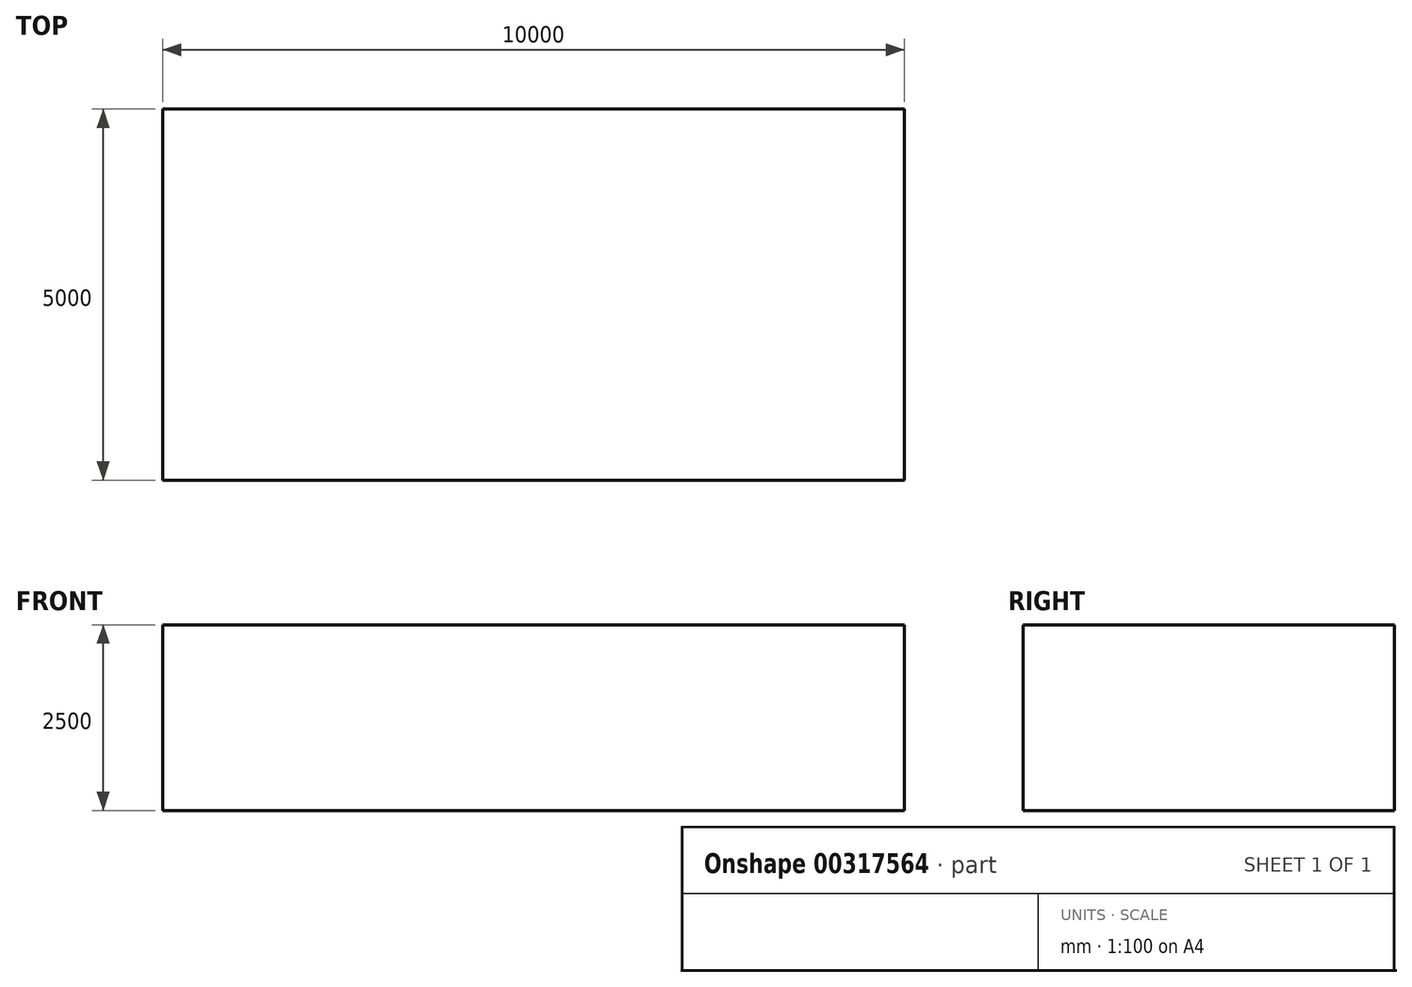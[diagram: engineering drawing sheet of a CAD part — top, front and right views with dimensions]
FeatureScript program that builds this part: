
annotation { "Feature Type Name" : "Feature", "Feature Type Description" : "" }
export const myFeature = defineFeature(function(context is Context, id is Id, definition is map)
    precondition{}
    {
        {
            var Q0;
            Q0=qCreatedBy(makeId("Front.planeOp"),FACE);
            var sketch = newSketch(context, id + "F0", { "sketchPlane" : qUnion([Q0])});
            skLineSegment(sketch, "E0.bottom", {"start": v(-4999.46, -1331.01) * mm, "end": v(5000.54, -1331.01) * mm});
            skLineSegment(sketch, "E0.top", {"start": v(-4999.46, -3831.01) * mm, "end": v(5000.54, -3831.01) * mm});
            skLineSegment(sketch, "E0.left", {"start": v(-4999.46, -1331.01) * mm, "end": v(-4999.46, -3831.01) * mm});
            skLineSegment(sketch, "E0.right", {"start": v(5000.54, -1331.01) * mm, "end": v(5000.54, -3831.01) * mm});
            skSolve(sketch);
        }
        {
            var Q0;
            Q0 = qSketchRegion(id + "F0", true);
            extrude(context, id + "F1", {"entities" : qUnion([Q0]), "depth" : 5000 * mm});
        }
    });
